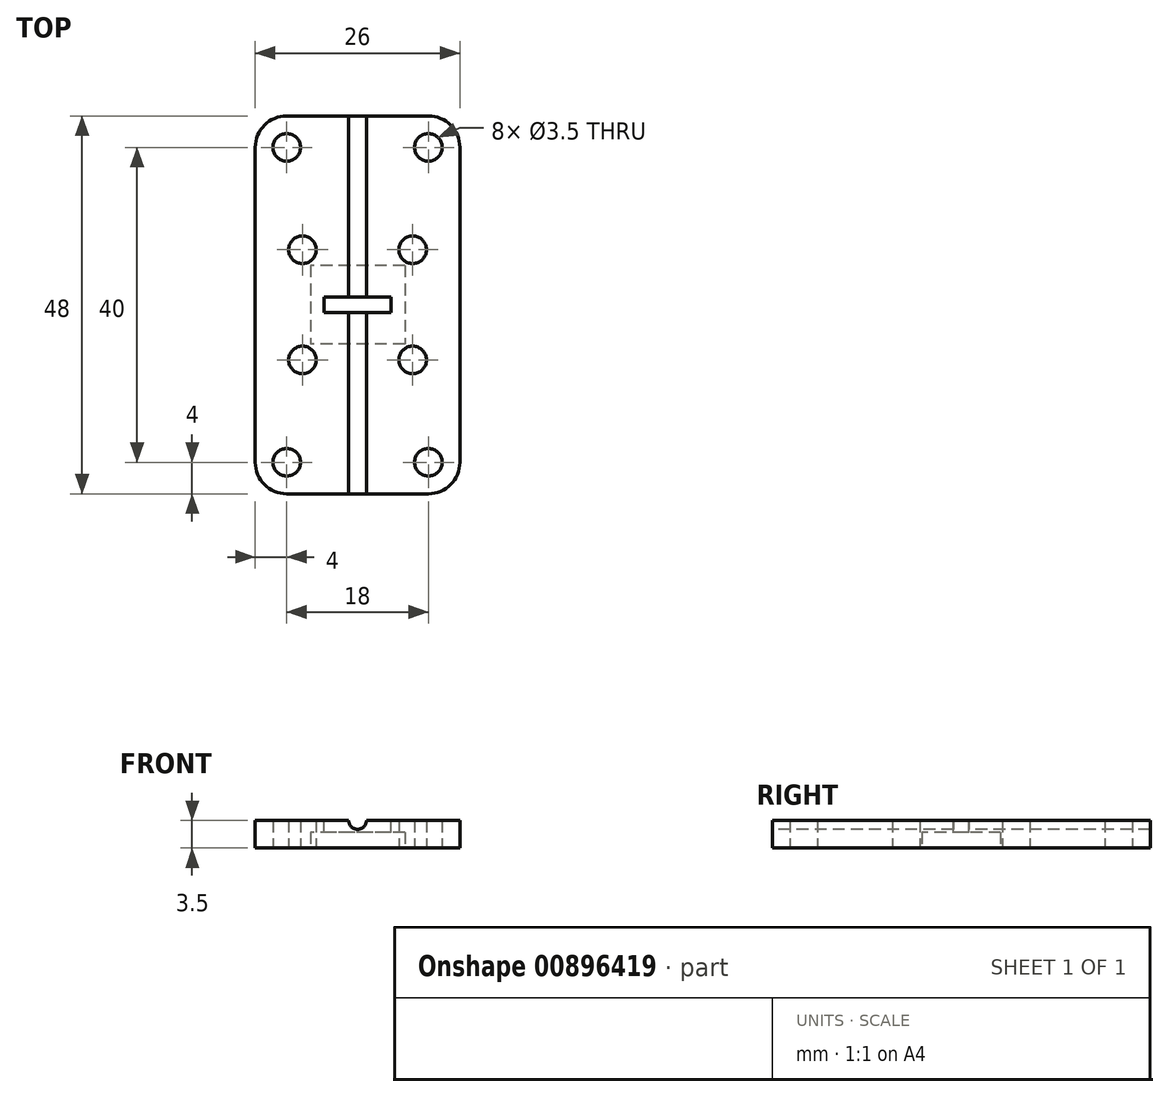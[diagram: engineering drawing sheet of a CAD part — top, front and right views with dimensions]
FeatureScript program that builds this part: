
annotation { "Feature Type Name" : "Feature", "Feature Type Description" : "" }
export const myFeature = defineFeature(function(context is Context, id is Id, definition is map)
    precondition{}
    {
        {
            var Q0;
            Q0=qCreatedBy(makeId("Top.planeOp"),FACE);
            var sketch = newSketch(context, id + "F0", { "sketchPlane" : qUnion([Q0])});
            skCircle(sketch, "E0", {"center": v(-7, 7) * mm, "radius": 1.75 * mm});
            skCircle(sketch, "E1", {"center": v(7, 7) * mm, "radius": 1.75 * mm});
            skCircle(sketch, "E2", {"center": v(7, -7) * mm, "radius": 1.75 * mm});
            skCircle(sketch, "E3", {"center": v(-7, -7) * mm, "radius": 1.75 * mm});
            skCircle(sketch, "E4", {"center": v(9, 20) * mm, "radius": 1.75 * mm});
            skCircle(sketch, "E5", {"center": v(-9, 20) * mm, "radius": 1.75 * mm});
            skCircle(sketch, "E6", {"center": v(-9, -20) * mm, "radius": 1.75 * mm});
            skCircle(sketch, "E7", {"center": v(9, -20) * mm, "radius": 1.75 * mm});
            skArc(sketch, "E8", {"start": v(-9, -24) * mm, "mid": v(-11.83, -22.83) * mm, "end": v(-13, -20) * mm});
            skArc(sketch, "E9", {"start": v(-13, 20) * mm, "mid": v(-11.83, 22.83) * mm, "end": v(-9, 24) * mm});
            skArc(sketch, "E10", {"start": v(9, 24) * mm, "mid": v(11.83, 22.83) * mm, "end": v(13, 20) * mm});
            skArc(sketch, "E11", {"start": v(13, -20) * mm, "mid": v(11.83, -22.83) * mm, "end": v(9, -24) * mm});
            skLineSegment(sketch, "E12", {"start": v(-13, -20) * mm, "end": v(-13, 20) * mm});
            skLineSegment(sketch, "E13", {"start": v(-9, 24) * mm, "end": v(9, 24) * mm});
            skLineSegment(sketch, "E14", {"start": v(13, 20) * mm, "end": v(13, -20) * mm});
            skLineSegment(sketch, "E15", {"start": v(9, -24) * mm, "end": v(-9, -24) * mm});
            skLineSegment(sketch, "E16.bottom", {"start": v(6, 5) * mm, "end": v(-6, 5) * mm});
            skLineSegment(sketch, "E16.top", {"start": v(6, -5) * mm, "end": v(-6, -5) * mm});
            skLineSegment(sketch, "E16.left", {"start": v(6, 5) * mm, "end": v(6, -5) * mm});
            skLineSegment(sketch, "E16.right", {"start": v(-6, 5) * mm, "end": v(-6, -5) * mm});
            skPoint(sketch, "E16.middle", {"position": v(0, 0) * mm});
            skSolve(sketch);
        }
        {
            var Q0;
            Q0 = qSketchRegion(id + "F0", true);
            extrude(context, id + "F1", {"entities" : qUnion([Q0]), "depth" : 2 * mm, "offsetDistance" : 25 * mm});
        }
        {
            var Q0;
            Q0=makeQuery(id+"F1.opExtrude","CAP_FACE",FACE,{"disambiguationData":[OSD([sQuery(id+"F0.wireOp",EDGE,"E0"),sQuery(id+"F0.wireOp",EDGE,"E1"),sQuery(id+"F0.wireOp",EDGE,"E2"),sQuery(id+"F0.wireOp",EDGE,"E3"),sQuery(id+"F0.wireOp",EDGE,"E4"),sQuery(id+"F0.wireOp",EDGE,"E5"),sQuery(id+"F0.wireOp",EDGE,"E6"),sQuery(id+"F0.wireOp",EDGE,"E7"),sQuery(id+"F0.wireOp",EDGE,"E8"),sQuery(id+"F0.wireOp",EDGE,"E9"),sQuery(id+"F0.wireOp",EDGE,"E10"),sQuery(id+"F0.wireOp",EDGE,"E11"),sQuery(id+"F0.wireOp",EDGE,"E12"),sQuery(id+"F0.wireOp",EDGE,"E13"),sQuery(id+"F0.wireOp",EDGE,"E14"),sQuery(id+"F0.wireOp",EDGE,"E15"),sQuery(id+"F0.wireOp",EDGE,"E16.bottom"),sQuery(id+"F0.wireOp",EDGE,"E16.top"),sQuery(id+"F0.wireOp",EDGE,"E16.left"),sQuery(id+"F0.wireOp",EDGE,"E16.right")])],"isStart":false});
            var sketch = newSketch(context, id + "F2", { "sketchPlane" : qUnion([Q0])});
            skCircle(sketch, "E17", {"center": v(-7, 7) * mm, "radius": 1.75 * mm});
            skCircle(sketch, "E18", {"center": v(7, -7) * mm, "radius": 1.75 * mm});
            skCircle(sketch, "E19", {"center": v(-7, -7) * mm, "radius": 1.75 * mm});
            skCircle(sketch, "E20", {"center": v(-9, -20) * mm, "radius": 1.75 * mm});
            skCircle(sketch, "E21", {"center": v(-9, 20) * mm, "radius": 1.75 * mm});
            skCircle(sketch, "E22", {"center": v(9, 20) * mm, "radius": 1.75 * mm});
            skCircle(sketch, "E23", {"center": v(9, -20) * mm, "radius": 1.75 * mm});
            skCircle(sketch, "E24", {"center": v(7, 7) * mm, "radius": 1.75 * mm});
            skArc(sketch, "E25", {"start": v(-9, -24) * mm, "mid": v(-11.83, -22.83) * mm, "end": v(-13, -20) * mm});
            skArc(sketch, "E26", {"start": v(-13, 20) * mm, "mid": v(-11.83, 22.83) * mm, "end": v(-9, 24) * mm});
            skArc(sketch, "E27", {"start": v(9, 24) * mm, "mid": v(11.83, 22.83) * mm, "end": v(13, 20) * mm});
            skArc(sketch, "E28", {"start": v(13, -20) * mm, "mid": v(11.83, -22.83) * mm, "end": v(9, -24) * mm});
            skLineSegment(sketch, "E29", {"start": v(-13, -20) * mm, "end": v(-13, 20) * mm});
            skLineSegment(sketch, "E30", {"start": v(-9, 24) * mm, "end": v(9, 24) * mm});
            skLineSegment(sketch, "E31", {"start": v(13, 20) * mm, "end": v(13, -20) * mm});
            skLineSegment(sketch, "E32", {"start": v(9, -24) * mm, "end": v(-9, -24) * mm});
            skSolve(sketch);
        }
        {
            var Q0;
            Q0 = qSketchRegion(id + "F2", true);
            extrude(context, id + "F3", {"entities" : qUnion([Q0]), "operationType" : NewBodyOperationType.ADD, "depth" : 1.5 * mm, "offsetDistance" : 25 * mm});
        }
        {
            var Q0;
            Q0=makeQuery(id+"F3.boolean.opBoolean","MERGE",FACE,{"derivedFrom":[makeQuery(id+"F1.opExtrude","SWEPT_FACE",FACE,{"disambiguationData":[OSD([sQuery(id+"F0.wireOp",EDGE,"E15")])]}),makeQuery(id+"F3.opExtrude","SWEPT_FACE",FACE,{"disambiguationData":[OSD([sQuery(id+"F2.wireOp",EDGE,"E32")])]})]});
            var sketch = newSketch(context, id + "F4", { "sketchPlane" : qUnion([Q0])});
            skCircle(sketch, "E33", {"center": v(0, 3.5) * mm, "radius": 1.13 * mm});
            skSolve(sketch);
        }
        {
            var Q0;
            Q0 = qSketchRegion(id + "F4", true);
            extrude(context, id + "F5", {"entities" : qUnion([Q0]), "depth" : -60 * mm, "offsetDistance" : 25 * mm});
        }
        {
            var Q0;
            Q0=makeQuery(id+"F3.opExtrude","CAP_FACE",FACE,{"disambiguationData":[OSD([sQuery(id+"F2.wireOp",EDGE,"E17"),sQuery(id+"F2.wireOp",EDGE,"E18"),sQuery(id+"F2.wireOp",EDGE,"E19"),sQuery(id+"F2.wireOp",EDGE,"E20"),sQuery(id+"F2.wireOp",EDGE,"E21"),sQuery(id+"F2.wireOp",EDGE,"E22"),sQuery(id+"F2.wireOp",EDGE,"E23"),sQuery(id+"F2.wireOp",EDGE,"E24"),sQuery(id+"F2.wireOp",EDGE,"E25"),sQuery(id+"F2.wireOp",EDGE,"E26"),sQuery(id+"F2.wireOp",EDGE,"E27"),sQuery(id+"F2.wireOp",EDGE,"E28"),sQuery(id+"F2.wireOp",EDGE,"E29"),sQuery(id+"F2.wireOp",EDGE,"E30"),sQuery(id+"F2.wireOp",EDGE,"E31"),sQuery(id+"F2.wireOp",EDGE,"E32")])],"isStart":false});
            var sketch = newSketch(context, id + "F6", { "sketchPlane" : qUnion([Q0])});
            skLineSegment(sketch, "E34.bottom", {"start": v(4.25, 1) * mm, "end": v(-4.25, 1) * mm});
            skLineSegment(sketch, "E34.top", {"start": v(4.25, -1) * mm, "end": v(-4.25, -1) * mm});
            skLineSegment(sketch, "E34.left", {"start": v(4.25, 1) * mm, "end": v(4.25, -1) * mm});
            skLineSegment(sketch, "E34.right", {"start": v(-4.25, 1) * mm, "end": v(-4.25, -1) * mm});
            skPoint(sketch, "E34.middle", {"position": v(0, 0) * mm});
            skSolve(sketch);
        }
        {
            var Q0;
            Q0 = qSketchRegion(id + "F6", true);
            extrude(context, id + "F7", {"entities" : qUnion([Q0]), "depth" : -5 * mm, "offsetDistance" : 25 * mm});
        }
        {
            var Q0;
            Q0=makeQuery(id+"F5.opExtrude","SWEPT_BODY",BODY,{"disambiguationData":[OSD([sQuery(id+"F4.wireOp",EDGE,"E33")])]});
            var Q1;
            Q1=makeQuery(id+"F7.opExtrude","SWEPT_BODY",BODY,{"disambiguationData":[OSD([sQuery(id+"F6.wireOp",EDGE,"E34.bottom"),sQuery(id+"F6.wireOp",EDGE,"E34.top"),sQuery(id+"F6.wireOp",EDGE,"E34.left"),sQuery(id+"F6.wireOp",EDGE,"E34.right")])]});
            var Q2;
            Q2=makeQuery(id+"F1.opExtrude","SWEPT_BODY",BODY,{"disambiguationData":[OSD([sQuery(id+"F0.wireOp",EDGE,"E0"),sQuery(id+"F0.wireOp",EDGE,"E1"),sQuery(id+"F0.wireOp",EDGE,"E2"),sQuery(id+"F0.wireOp",EDGE,"E3"),sQuery(id+"F0.wireOp",EDGE,"E4"),sQuery(id+"F0.wireOp",EDGE,"E5"),sQuery(id+"F0.wireOp",EDGE,"E6"),sQuery(id+"F0.wireOp",EDGE,"E7"),sQuery(id+"F0.wireOp",EDGE,"E8"),sQuery(id+"F0.wireOp",EDGE,"E9"),sQuery(id+"F0.wireOp",EDGE,"E10"),sQuery(id+"F0.wireOp",EDGE,"E11"),sQuery(id+"F0.wireOp",EDGE,"E12"),sQuery(id+"F0.wireOp",EDGE,"E13"),sQuery(id+"F0.wireOp",EDGE,"E14"),sQuery(id+"F0.wireOp",EDGE,"E15"),sQuery(id+"F0.wireOp",EDGE,"E16.bottom"),sQuery(id+"F0.wireOp",EDGE,"E16.top"),sQuery(id+"F0.wireOp",EDGE,"E16.left"),sQuery(id+"F0.wireOp",EDGE,"E16.right")])]});
            booleanBodies(context, id + "F8", {"operationType" : BooleanOperationType.SUBTRACTION, "tools" : qUnion([Q0, Q1]), "targets" : qUnion([Q2])});
        }
    });
